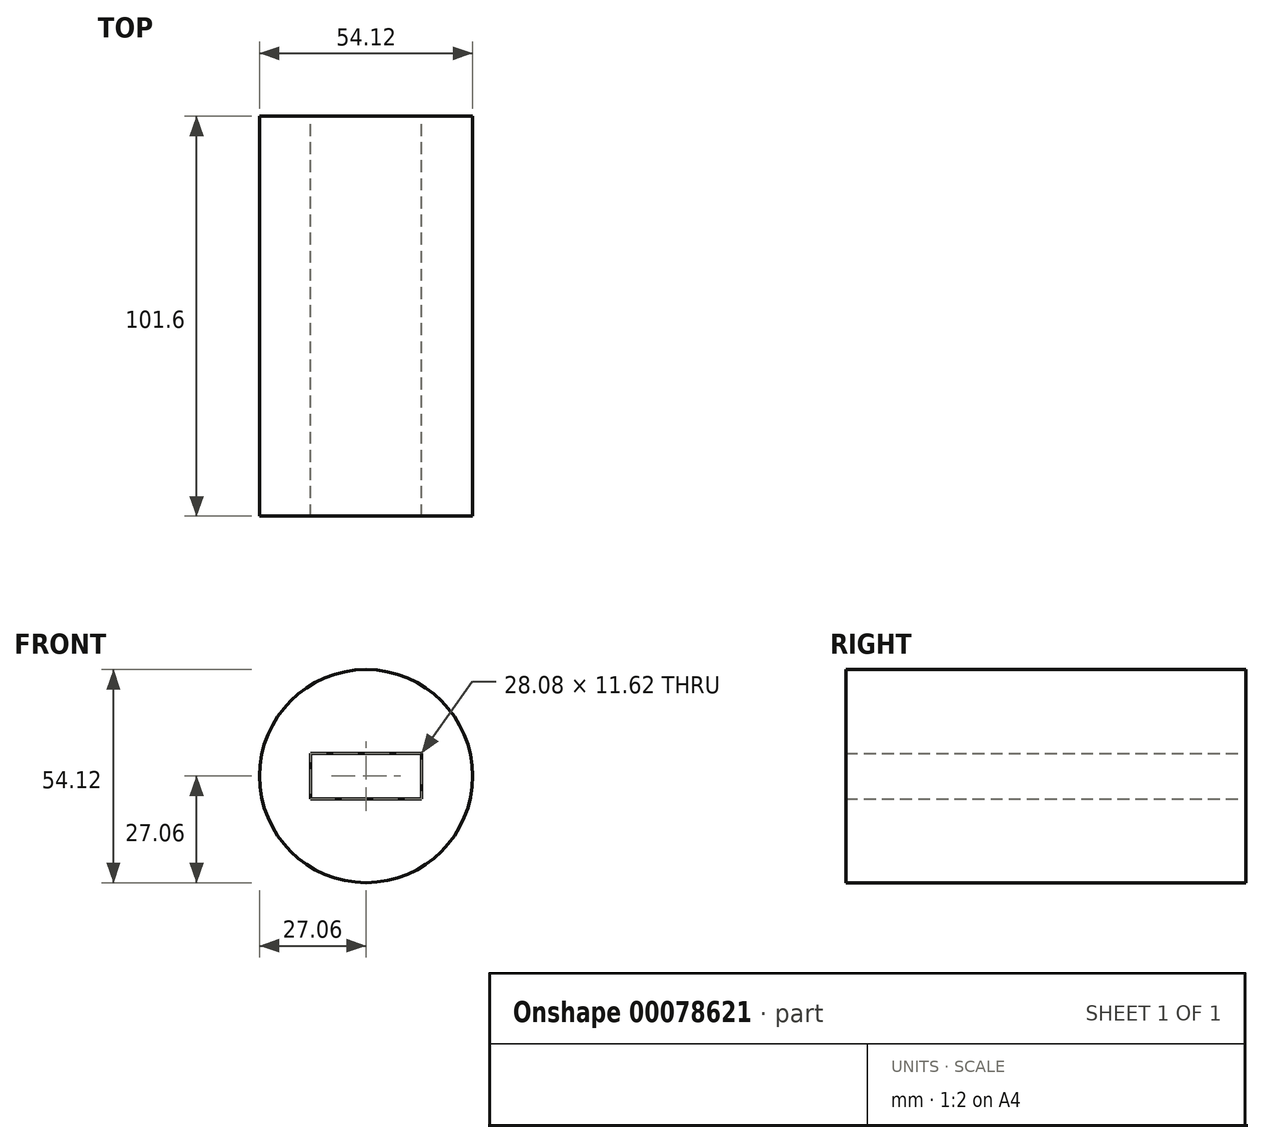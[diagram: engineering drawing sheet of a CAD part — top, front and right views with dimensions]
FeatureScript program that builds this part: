
annotation { "Feature Type Name" : "Feature", "Feature Type Description" : "" }
export const myFeature = defineFeature(function(context is Context, id is Id, definition is map)
    precondition{}
    {
        {
            var Q0;
            Q0=qCreatedBy(makeId("Front.planeOp"),FACE);
            var sketch = newSketch(context, id + "F0", { "sketchPlane" : qUnion([Q0])});
            skCircle(sketch, "E0", {"center": v(0, 0) * mm, "radius": 27.06 * mm});
            skLineSegment(sketch, "E1.bottom", {"start": v(14.04, -5.8) * mm, "end": v(-14.04, -5.8) * mm});
            skLineSegment(sketch, "E1.top", {"start": v(14.04, 5.8) * mm, "end": v(-14.04, 5.8) * mm});
            skLineSegment(sketch, "E1.left", {"start": v(14.04, -5.8) * mm, "end": v(14.04, 5.8) * mm});
            skLineSegment(sketch, "E1.right", {"start": v(-14.04, -5.8) * mm, "end": v(-14.04, 5.8) * mm});
            skSolve(sketch);
        }
        {
            var Q0;
            Q0=makeQuery(id+"F0.imprint","IMPRINT",FACE,{"disambiguationData":[TD([[makeQuery(id+"F0.imprint","IMPRINT",EDGE,{"derivedFrom":sQuery(id+"F0.wireOp",EDGE,"E0")}),1.0]])]});
            extrude(context, id + "F1", {"entities" : qUnion([Q0]), "depth" : 101.6 * mm});
        }
    });
